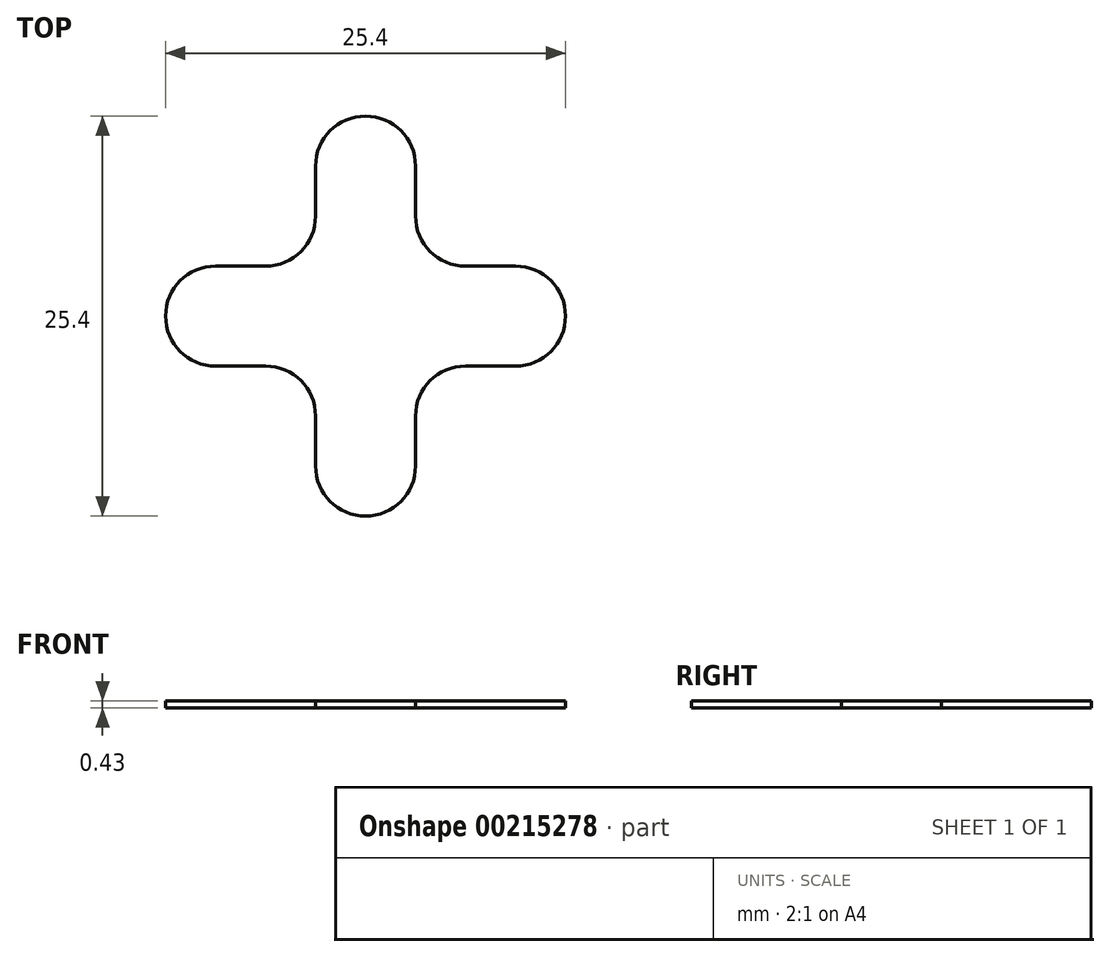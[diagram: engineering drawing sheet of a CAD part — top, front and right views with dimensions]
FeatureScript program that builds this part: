
annotation { "Feature Type Name" : "Feature", "Feature Type Description" : "" }
export const myFeature = defineFeature(function(context is Context, id is Id, definition is map)
    precondition{}
    {
        {
            var Q0;
            Q0=qCreatedBy(makeId("Top.planeOp"),FACE);
            var sketch = newSketch(context, id + "F0", { "sketchPlane" : qUnion([Q0])});
            skLineSegment(sketch, "E0.bottom", {"start": v(0, -12.7) * mm, "end": v(0, -12.7) * mm});
            skLineSegment(sketch, "E0.top", {"start": v(0, 12.7) * mm, "end": v(0, 12.7) * mm});
            skLineSegment(sketch, "E0.left", {"start": v(3.17, -9.53) * mm, "end": v(3.17, -6.35) * mm});
            skLineSegment(sketch, "E0.right", {"start": v(-3.18, -9.53) * mm, "end": v(-3.18, -6.35) * mm});
            skPoint(sketch, "E0.middle", {"position": v(0, 0) * mm});
            skLineSegment(sketch, "E1.bottom", {"start": v(9.53, 3.18) * mm, "end": v(6.35, 3.18) * mm});
            skLineSegment(sketch, "E1.top", {"start": v(9.53, -3.17) * mm, "end": v(6.35, -3.17) * mm});
            skLineSegment(sketch, "E1.left", {"start": v(12.7, 0) * mm, "end": v(12.7, 0) * mm});
            skLineSegment(sketch, "E1.right", {"start": v(-12.7, 0) * mm, "end": v(-12.7, 0) * mm});
            skLineSegment(sketch, "E2.trimOffspring", {"start": v(-6.35, 3.17) * mm, "end": v(-9.53, 3.17) * mm});
            skLineSegment(sketch, "E3.trimOffspring", {"start": v(3.18, 6.35) * mm, "end": v(3.18, 9.53) * mm});
            skLineSegment(sketch, "E4.trimOffspring", {"start": v(-6.35, -3.18) * mm, "end": v(-9.53, -3.18) * mm});
            skLineSegment(sketch, "E5.trimOffspring", {"start": v(-3.17, 6.35) * mm, "end": v(-3.17, 9.53) * mm});
            skPoint(sketch, "E6.visualSharp", {"position": v(-12.7, 3.17) * mm});
            skArc(sketch, "E6.filletArc", {"start": v(-9.53, 3.17) * mm, "mid": v(-11.77, 2.25) * mm, "end": v(-12.7, 0) * mm});
            skPoint(sketch, "E7.visualSharp", {"position": v(-12.7, -3.18) * mm});
            skArc(sketch, "E7.filletArc", {"start": v(-12.7, 0) * mm, "mid": v(-11.77, -2.25) * mm, "end": v(-9.53, -3.18) * mm});
            skPoint(sketch, "E8.visualSharp", {"position": v(-3.18, -12.7) * mm});
            skArc(sketch, "E8.filletArc", {"start": v(-3.18, -9.53) * mm, "mid": v(-2.25, -11.77) * mm, "end": v(0, -12.7) * mm});
            skPoint(sketch, "E9.visualSharp", {"position": v(3.17, -12.7) * mm});
            skArc(sketch, "E9.filletArc", {"start": v(0, -12.7) * mm, "mid": v(2.25, -11.77) * mm, "end": v(3.17, -9.53) * mm});
            skPoint(sketch, "E10.visualSharp", {"position": v(3.18, -3.17) * mm});
            skArc(sketch, "E10.filletArc", {"start": v(6.35, -3.17) * mm, "mid": v(4.1, -4.1) * mm, "end": v(3.18, -6.35) * mm});
            skPoint(sketch, "E11.visualSharp", {"position": v(-3.18, -3.18) * mm});
            skArc(sketch, "E11.filletArc", {"start": v(-3.18, -6.35) * mm, "mid": v(-4.1, -4.1) * mm, "end": v(-6.35, -3.18) * mm});
            skPoint(sketch, "E12.visualSharp", {"position": v(12.7, -3.17) * mm});
            skArc(sketch, "E12.filletArc", {"start": v(9.53, -3.17) * mm, "mid": v(11.77, -2.25) * mm, "end": v(12.7, 0) * mm});
            skPoint(sketch, "E13.visualSharp", {"position": v(12.7, 3.18) * mm});
            skArc(sketch, "E13.filletArc", {"start": v(12.7, 0) * mm, "mid": v(11.77, 2.25) * mm, "end": v(9.53, 3.18) * mm});
            skPoint(sketch, "E14.visualSharp", {"position": v(3.18, 3.18) * mm});
            skArc(sketch, "E14.filletArc", {"start": v(3.18, 6.35) * mm, "mid": v(4.1, 4.1) * mm, "end": v(6.35, 3.18) * mm});
            skPoint(sketch, "E15.visualSharp", {"position": v(3.18, 12.7) * mm});
            skArc(sketch, "E15.filletArc", {"start": v(3.18, 9.53) * mm, "mid": v(2.25, 11.77) * mm, "end": v(0, 12.7) * mm});
            skPoint(sketch, "E16.visualSharp", {"position": v(-3.17, 12.7) * mm});
            skArc(sketch, "E16.filletArc", {"start": v(0, 12.7) * mm, "mid": v(-2.25, 11.77) * mm, "end": v(-3.17, 9.53) * mm});
            skPoint(sketch, "E17.visualSharp", {"position": v(-3.18, 3.17) * mm});
            skArc(sketch, "E17.filletArc", {"start": v(-6.35, 3.17) * mm, "mid": v(-4.1, 4.1) * mm, "end": v(-3.18, 6.35) * mm});
            skSolve(sketch);
        }
        {
            var Q0;
            Q0 = qSketchRegion(id + "F0", true);
            extrude(context, id + "F1", {"entities" : qUnion([Q0]), "depth" : 0.43 * mm, "offsetDistance" : 25.4 * mm});
        }
    });
